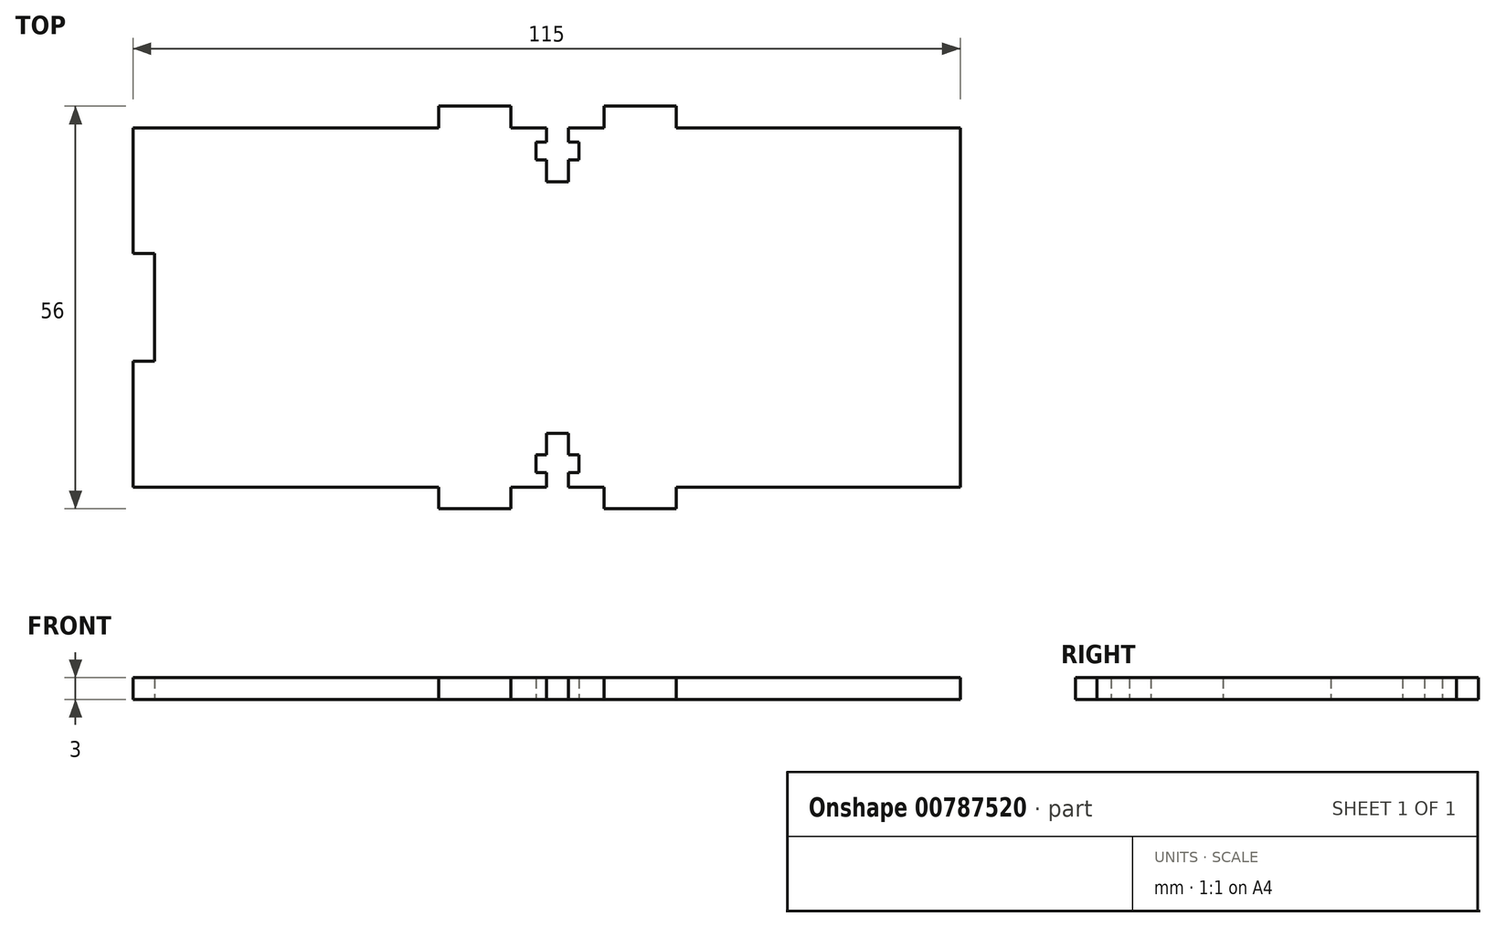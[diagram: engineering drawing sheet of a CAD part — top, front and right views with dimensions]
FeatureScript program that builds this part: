
annotation { "Feature Type Name" : "Feature", "Feature Type Description" : "" }
export const myFeature = defineFeature(function(context is Context, id is Id, definition is map)
    precondition{}
    {
        {
            var Q0;
            Q0=qCreatedBy(makeId("Top.planeOp"),FACE);
            var sketch = newSketch(context, id + "F0", { "sketchPlane" : qUnion([Q0])});
            skLineSegment(sketch, "E0.bottom", {"start": v(-118.94, -27.28) * mm, "end": v(-76.44, -27.28) * mm});
            skLineSegment(sketch, "E0.top", {"start": v(-118.94, -77.28) * mm, "end": v(-76.44, -77.28) * mm});
            skLineSegment(sketch, "E0.left", {"start": v(-118.94, -27.28) * mm, "end": v(-118.94, -44.78) * mm});
            skLineSegment(sketch, "E0.right", {"start": v(-3.94, -27.28) * mm, "end": v(-3.94, -77.28) * mm});
            skLineSegment(sketch, "E1.bottom", {"start": v(-118.94, -44.78) * mm, "end": v(-115.94, -44.78) * mm});
            skLineSegment(sketch, "E1.top", {"start": v(-118.94, -59.78) * mm, "end": v(-115.94, -59.78) * mm});
            skLineSegment(sketch, "E1.right", {"start": v(-115.94, -44.78) * mm, "end": v(-115.94, -59.78) * mm});
            skPoint(sketch, "E1.middle", {"position": v(-118.94, -52.28) * mm});
            skLineSegment(sketch, "E2.trimOffspring", {"start": v(-118.94, -59.78) * mm, "end": v(-118.94, -77.28) * mm});
            skLineSegment(sketch, "E3.0", {"start": v(-59.94, -27.28) * mm, "end": v(-59.94, -77.28) * mm, "construction": true});
            skLineSegment(sketch, "E4", {"start": v(-58.44, -27.28) * mm, "end": v(-58.44, -29.28) * mm});
            skLineSegment(sketch, "E5", {"start": v(-58.44, -29.28) * mm, "end": v(-56.94, -29.28) * mm});
            skLineSegment(sketch, "E6", {"start": v(-56.94, -29.28) * mm, "end": v(-56.94, -31.78) * mm});
            skLineSegment(sketch, "E7", {"start": v(-56.94, -31.78) * mm, "end": v(-58.44, -31.78) * mm});
            skLineSegment(sketch, "E8", {"start": v(-58.44, -31.78) * mm, "end": v(-58.44, -34.78) * mm});
            skLineSegment(sketch, "E9", {"start": v(-58.44, -34.78) * mm, "end": v(-61.44, -34.78) * mm});
            skLineSegment(sketch, "E10", {"start": v(-61.44, -34.78) * mm, "end": v(-61.44, -31.78) * mm});
            skLineSegment(sketch, "E11", {"start": v(-61.44, -31.78) * mm, "end": v(-62.94, -31.78) * mm});
            skLineSegment(sketch, "E12", {"start": v(-62.94, -31.78) * mm, "end": v(-62.94, -29.28) * mm});
            skLineSegment(sketch, "E13", {"start": v(-62.94, -29.28) * mm, "end": v(-61.44, -29.28) * mm});
            skLineSegment(sketch, "E14", {"start": v(-61.44, -29.28) * mm, "end": v(-61.44, -27.28) * mm});
            skLineSegment(sketch, "E15", {"start": v(-53.44, -27.28) * mm, "end": v(-53.44, -24.28) * mm});
            skLineSegment(sketch, "E16", {"start": v(-53.44, -24.28) * mm, "end": v(-43.44, -24.28) * mm});
            skLineSegment(sketch, "E17", {"start": v(-43.44, -24.28) * mm, "end": v(-43.44, -27.28) * mm});
            skLineSegment(sketch, "E18", {"start": v(-66.44, -27.28) * mm, "end": v(-66.44, -24.28) * mm});
            skLineSegment(sketch, "E19", {"start": v(-66.44, -24.28) * mm, "end": v(-76.44, -24.28) * mm});
            skLineSegment(sketch, "E20", {"start": v(-76.44, -24.28) * mm, "end": v(-76.44, -27.28) * mm});
            skLineSegment(sketch, "E21", {"start": v(-61.44, -77.28) * mm, "end": v(-61.44, -75.28) * mm});
            skLineSegment(sketch, "E22", {"start": v(-61.44, -75.28) * mm, "end": v(-62.94, -75.28) * mm});
            skLineSegment(sketch, "E23", {"start": v(-62.94, -75.28) * mm, "end": v(-62.94, -72.78) * mm});
            skLineSegment(sketch, "E24", {"start": v(-62.94, -72.78) * mm, "end": v(-61.44, -72.78) * mm});
            skLineSegment(sketch, "E25", {"start": v(-61.44, -72.78) * mm, "end": v(-61.44, -69.78) * mm});
            skLineSegment(sketch, "E26", {"start": v(-61.44, -69.78) * mm, "end": v(-58.44, -69.78) * mm});
            skLineSegment(sketch, "E27", {"start": v(-58.44, -69.78) * mm, "end": v(-58.44, -72.78) * mm});
            skLineSegment(sketch, "E28", {"start": v(-58.44, -72.78) * mm, "end": v(-56.94, -72.78) * mm});
            skLineSegment(sketch, "E29", {"start": v(-56.94, -72.78) * mm, "end": v(-56.94, -75.28) * mm});
            skLineSegment(sketch, "E30", {"start": v(-56.94, -75.28) * mm, "end": v(-58.44, -75.28) * mm});
            skLineSegment(sketch, "E31", {"start": v(-58.44, -75.28) * mm, "end": v(-58.44, -77.28) * mm});
            skLineSegment(sketch, "E32", {"start": v(-66.44, -77.28) * mm, "end": v(-66.44, -80.28) * mm});
            skLineSegment(sketch, "E33", {"start": v(-66.44, -80.28) * mm, "end": v(-76.44, -80.28) * mm});
            skLineSegment(sketch, "E34", {"start": v(-76.44, -80.28) * mm, "end": v(-76.44, -77.28) * mm});
            skLineSegment(sketch, "E35", {"start": v(-53.44, -77.28) * mm, "end": v(-53.44, -80.28) * mm});
            skLineSegment(sketch, "E36", {"start": v(-53.44, -80.28) * mm, "end": v(-43.44, -80.28) * mm});
            skLineSegment(sketch, "E37", {"start": v(-43.44, -80.28) * mm, "end": v(-43.44, -77.28) * mm});
            skLineSegment(sketch, "E38.trimOffspring", {"start": v(-66.44, -27.28) * mm, "end": v(-61.44, -27.28) * mm});
            skLineSegment(sketch, "E39.trimOffspring", {"start": v(-43.44, -27.28) * mm, "end": v(-3.94, -27.28) * mm});
            skLineSegment(sketch, "E40.trimOffspring", {"start": v(-43.44, -77.28) * mm, "end": v(-3.94, -77.28) * mm});
            skLineSegment(sketch, "E41.trimOffspring", {"start": v(-66.44, -77.28) * mm, "end": v(-61.44, -77.28) * mm});
            skLineSegment(sketch, "E42.trimOffspring", {"start": v(-58.44, -77.28) * mm, "end": v(-53.44, -77.28) * mm});
            skLineSegment(sketch, "E43.trimOffspring", {"start": v(-58.44, -27.28) * mm, "end": v(-53.44, -27.28) * mm});
            skSolve(sketch);
        }
        {
            var Q0;
            Q0=makeQuery(id+"F0.imprint","IMPRINT",FACE,{"disambiguationData":[TD([[makeQuery(id+"F0.imprint","IMPRINT",EDGE,{"derivedFrom":sQuery(id+"F0.wireOp",EDGE,"E0.bottom")}),-1.0]])]});
            extrude(context, id + "F1", {"entities" : qUnion([Q0]), "depth" : 3 * mm, "offsetDistance" : 25.4 * mm});
        }
    });
